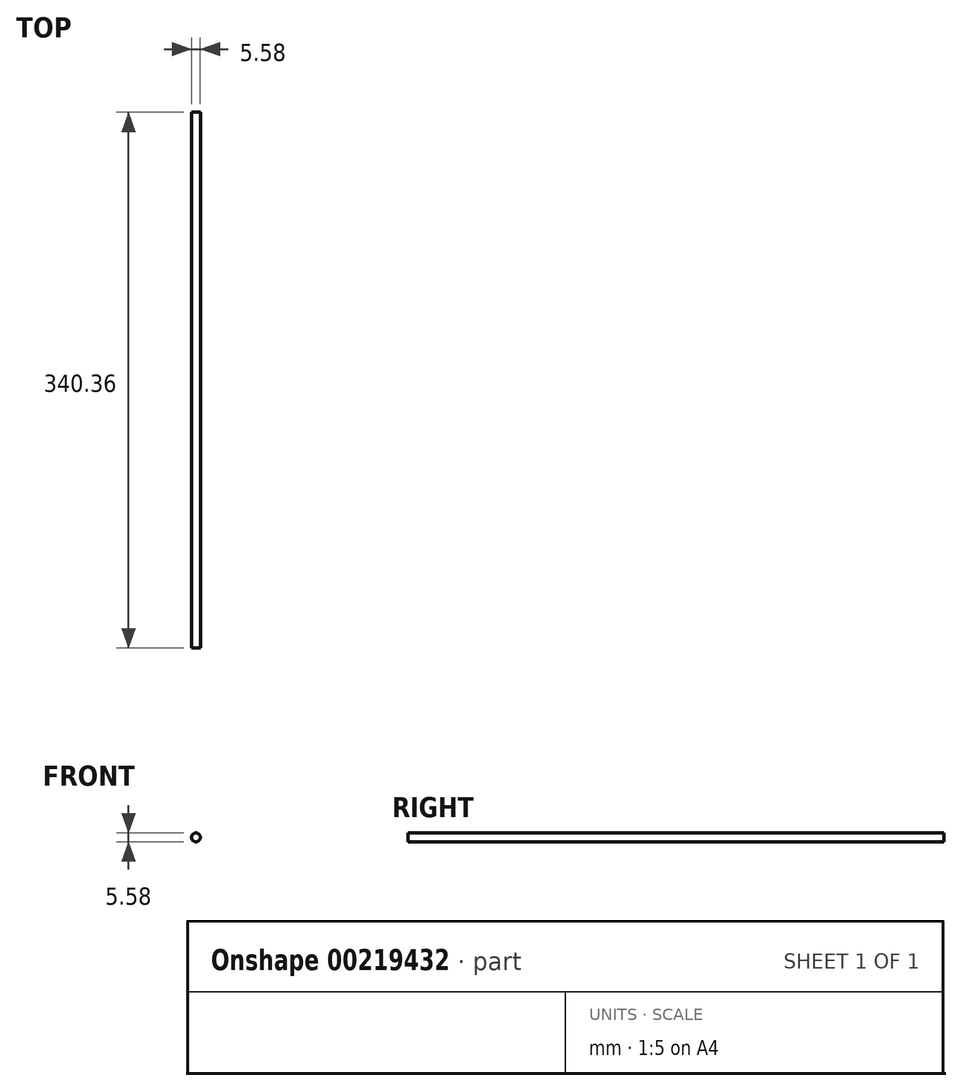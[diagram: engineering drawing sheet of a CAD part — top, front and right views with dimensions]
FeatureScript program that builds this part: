
annotation { "Feature Type Name" : "Feature", "Feature Type Description" : "" }
export const myFeature = defineFeature(function(context is Context, id is Id, definition is map)
    precondition{}
    {
        {
            var Q0;
            Q0=qCreatedBy(makeId("Front.planeOp"),FACE);
            var sketch = newSketch(context, id + "F0", { "sketchPlane" : qUnion([Q0])});
            skCircle(sketch, "E0", {"center": v(0, 0) * mm, "radius": 2.8 * mm});
            skSolve(sketch);
        }
        {
            var Q0;
            Q0=makeQuery(id+"F0.imprint","IMPRINT",FACE,{"disambiguationData":[TD([[makeQuery(id+"F0.imprint","IMPRINT",EDGE,{"derivedFrom":sQuery(id+"F0.wireOp",EDGE,"E0")}),1.0]])]});
            extrude(context, id + "F1", {"entities" : qUnion([Q0]), "depth" : 340.36 * mm, "offsetDistance" : 25.4 * mm});
        }
    });
